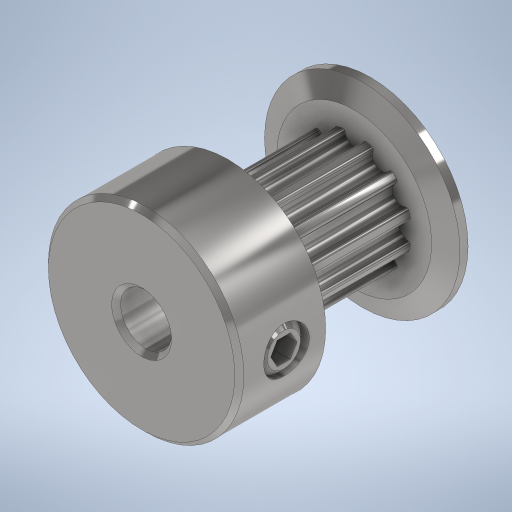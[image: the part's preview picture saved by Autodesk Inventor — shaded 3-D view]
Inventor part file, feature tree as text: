
AUTODESK INVENTOR PART (.ipt)
format: ipt  version: 2023 (Build 270158000, 158)  size: 391,680 bytes
history: native  units: in
note: dims shown in document units (in); Inventor stores cm internally (conversion verified against a paired STEP export)
features: chamfer x1
ambient origin geometry x8: Origin, YZ Plane, XZ Plane, XY Plane, X Axis, Y Axis, Z Axis, Center Point
bodies: Solid1 (feature_tree)
feature tree (1):
  chamfer  "Chamfer1"  [1 undecoded]
note: 1 required parameter value undecoded (feature->parameter linkage not recoverable at this tier; creation-order binding heuristic only, values carry confidence <= 0.55)
